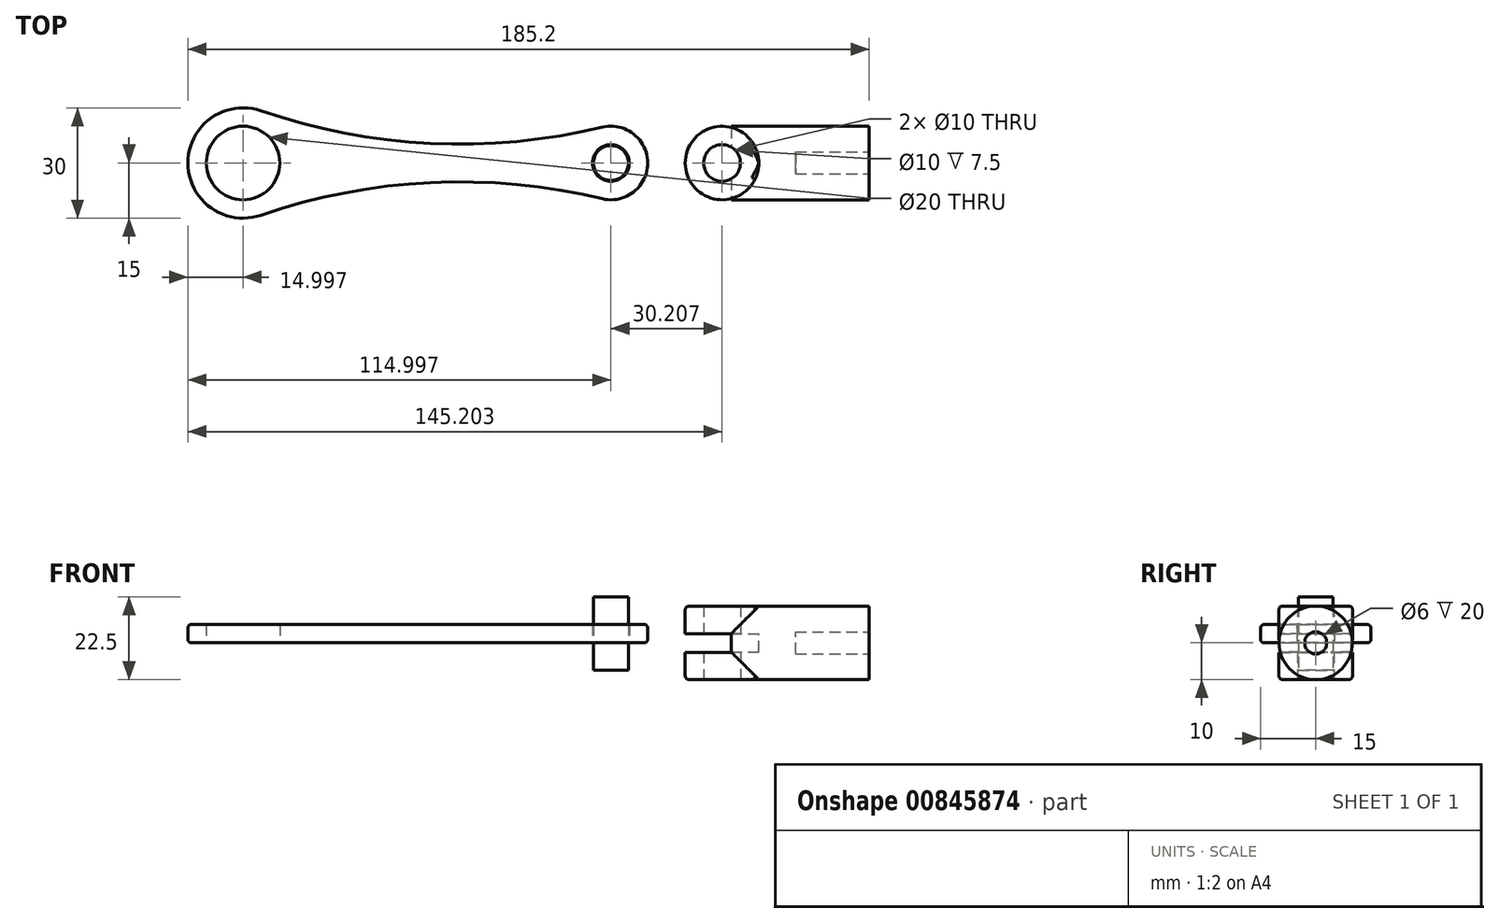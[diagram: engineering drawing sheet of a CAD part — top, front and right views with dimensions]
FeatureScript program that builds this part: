
annotation { "Feature Type Name" : "Feature", "Feature Type Description" : "" }
export const myFeature = defineFeature(function(context is Context, id is Id, definition is map)
    precondition{}
    {
        {
            var Q0;
            Q0=qCreatedBy(makeId("Top.planeOp"),FACE);
            var sketch = newSketch(context, id + "F0", { "sketchPlane" : qUnion([Q0])});
            skCircle(sketch, "E0", {"center": v(-57.77, 0) * mm, "radius": 10 * mm});
            skCircle(sketch, "E1", {"center": v(-57.77, 0) * mm, "radius": 15 * mm});
            skCircle(sketch, "E2", {"center": v(42.23, 0) * mm, "radius": 5 * mm});
            skCircle(sketch, "E3", {"center": v(42.23, 0) * mm, "radius": 10 * mm});
            skArc(sketch, "E4", {"start": v(-52.9, 14.18) * mm, "mid": v(-6.82, 5.33) * mm, "end": v(39.9, 9.72) * mm});
            skArc(sketch, "E5.MirrorCS", {"start": v(-52.9, -14.18) * mm, "mid": v(-6.82, -5.33) * mm, "end": v(39.9, -9.72) * mm});
            skCircle(sketch, "E6", {"center": v(42.23, 0) * mm, "radius": 4.75 * mm});
            skCircle(sketch, "E7", {"center": v(72.43, 0) * mm, "radius": 10 * mm});
            skCircle(sketch, "E8", {"center": v(72.43, 0) * mm, "radius": 5 * mm});
            skLineSegment(sketch, "E9", {"start": v(82.43, 0) * mm, "end": v(112.43, 0) * mm});
            skLineSegment(sketch, "E10", {"start": v(72.43, 10) * mm, "end": v(112.43, 10) * mm});
            skLineSegment(sketch, "E11", {"start": v(112.43, 10) * mm, "end": v(112.43, 0) * mm});
            skSolve(sketch);
        }
        {
            var Q0;
            Q0=makeQuery(id+"F0.imprint","IMPRINT",FACE,{"disambiguationData":[TD([[makeQuery(id+"F0.imprint","IMPRINT",EDGE,{"derivedFrom":sQuery(id+"F0.wireOp",EDGE,"E2")}),-1.0]])]});
            var Q1;
            {var subQ0=sQuery(id+"F0.wireOp",EDGE,"E4");Q1=makeQuery(id+"F0.imprint","IMPRINT",FACE,{"disambiguationData":[TD([[makeQuery(id+"F0.imprint","IMPRINT",EDGE,{"derivedFrom":subQ0}),-1.0]])]});}
            var Q2;
            Q2=makeQuery(id+"F0.imprint","IMPRINT",FACE,{"disambiguationData":[TD([[makeQuery(id+"F0.imprint","IMPRINT",EDGE,{"derivedFrom":sQuery(id+"F0.wireOp",EDGE,"E0")}),-1.0]])]});
            extrude(context, id + "F1", {"entities" : qUnion([Q0, Q1, Q2]), "depth" : 5 * mm, "offsetDistance" : 25 * mm});
        }
        {
            var Q0;
            Q0=makeQuery(id+"F1.opExtrude","CAP_EDGE",EDGE,{"disambiguationData":[OSD([sQuery(id+"F0.wireOp",EDGE,"E4")])],"isStart":false});
            var Q1;
            Q1=makeQuery(id+"F1.opExtrude","CAP_EDGE",EDGE,{"disambiguationData":[OSD([sQuery(id+"F0.wireOp",EDGE,"E1")])],"isStart":false});
            var Q2;
            Q2=makeQuery(id+"F1.opExtrude","CAP_EDGE",EDGE,{"disambiguationData":[OSD([sQuery(id+"F0.wireOp",EDGE,"E5.MirrorCS")])],"isStart":false});
            var Q3;
            Q3=makeQuery(id+"F1.opExtrude","CAP_EDGE",EDGE,{"disambiguationData":[OSD([sQuery(id+"F0.wireOp",EDGE,"E3")])],"isStart":false});
            fillet(context, id + "F2", {"entities" : qUnion([Q0, Q1, Q2, Q3]), "radius" : 1 * mm, "tangentPropagation" : true, "allowEdgeOverflow" : false});
        }
        {
            var Q0;
            Q0=makeQuery(id+"F1.opExtrude","CAP_EDGE",EDGE,{"disambiguationData":[OSD([sQuery(id+"F0.wireOp",EDGE,"E4")])],"isStart":true});
            var Q1;
            Q1=makeQuery(id+"F1.opExtrude","CAP_EDGE",EDGE,{"disambiguationData":[OSD([sQuery(id+"F0.wireOp",EDGE,"E1")])],"isStart":true});
            var Q2;
            Q2=makeQuery(id+"F1.opExtrude","CAP_EDGE",EDGE,{"disambiguationData":[OSD([sQuery(id+"F0.wireOp",EDGE,"E5.MirrorCS")])],"isStart":true});
            var Q3;
            Q3=makeQuery(id+"F1.opExtrude","CAP_EDGE",EDGE,{"disambiguationData":[OSD([sQuery(id+"F0.wireOp",EDGE,"E3")])],"isStart":true});
            fillet(context, id + "F3", {"entities" : qUnion([Q0, Q1, Q2, Q3]), "radius" : 1 * mm, "tangentPropagation" : true, "allowEdgeOverflow" : false});
        }
        {
            var Q0;
            Q0=makeQuery(id+"F0.imprint","IMPRINT",FACE,{"disambiguationData":[TD([[makeQuery(id+"F0.imprint","IMPRINT",EDGE,{"derivedFrom":sQuery(id+"F0.wireOp",EDGE,"E6")}),1.0]])]});
            extrude(context, id + "F4", {"entities" : qUnion([Q0]), "depth" : 12.5 * mm, "offsetDistance" : 25 * mm, "hasSecondDirection" : true, "secondDirectionOppositeDirection" : true, "secondDirectionDepth" : 7.5 * mm});
        }
        {
            var Q0;
            Q0=makeQuery(id+"F0.imprint","IMPRINT",FACE,{"disambiguationData":[TD([[makeQuery(id+"F0.imprint","IMPRINT",EDGE,{"derivedFrom":sQuery(id+"F0.wireOp",EDGE,"E8")}),-1.0]])]});
            extrude(context, id + "F5", {"entities" : qUnion([Q0]), "depth" : 2.5 * mm, "offsetDistance" : 25 * mm, "hasSecondDirection" : true, "secondDirectionOppositeDirection" : true, "secondDirectionDepth" : 2.5 * mm});
        }
        {
            var Q0;
            Q0=makeQuery(id+"F5.opExtrude","CAP_FACE",FACE,{"disambiguationData":[OSD([sQuery(id+"F0.wireOp",EDGE,"E7"),sQuery(id+"F0.wireOp",EDGE,"E8")])],"isStart":false});
            extrude(context, id + "F6", {"entities" : qUnion([Q0]), "depth" : 7.5 * mm, "offsetDistance" : 25 * mm});
        }
        {
            var Q0;
            Q0=makeQuery(id+"F5.opExtrude","CAP_FACE",FACE,{"disambiguationData":[OSD([sQuery(id+"F0.wireOp",EDGE,"E7"),sQuery(id+"F0.wireOp",EDGE,"E8")])],"isStart":true});
            extrude(context, id + "F7", {"entities" : qUnion([Q0]), "operationType" : NewBodyOperationType.ADD, "depth" : 7.5 * mm, "offsetDistance" : 25 * mm});
        }
        {
            var Q0;
            {var subQ0=sQuery(id+"F0.wireOp",EDGE,"E9");Q0=makeQuery(id+"F0.imprint","IMPRINT",FACE,{"disambiguationData":[TD([[makeQuery(id+"F0.imprint","IMPRINT",EDGE,{"derivedFrom":subQ0}),1.0]])]});}
            var Q1;
            Q1=sQuery(id+"F0.wireOp",EDGE,"E9");
            revolve(context, id + "F8", {"operationType" : NewBodyOperationType.ADD, "surfaceOperationType" : NewSurfaceOperationType.NEW, "entities" : qUnion([Q0]), "axis" : qUnion([Q1]), "revolveType" : RevolveType.FULL});
        }
        {
            var Q0;
            Q0=makeQuery(id+"F0.imprint","IMPRINT",FACE,{"disambiguationData":[TD([[makeQuery(id+"F0.imprint","IMPRINT",EDGE,{"derivedFrom":sQuery(id+"F0.wireOp",EDGE,"E8")}),-1.0]])]});
            extrude(context, id + "F9", {"entities" : qUnion([Q0]), "operationType" : NewBodyOperationType.REMOVE, "oppositeDirection" : true, "depth" : 2.5 * mm, "offsetDistance" : 25 * mm, "hasSecondDirection" : true, "secondDirectionOppositeDirection" : false, "secondDirectionDepth" : 2.5 * mm});
        }
        {
            var Q0;
            Q0=qCreatedBy(makeId("Front.planeOp"),FACE);
            cPlane(context, id + "F10", {"entities" : qUnion([Q0]), "cplaneType" : CPlaneType.OFFSET, "offset" : 10 * mm, "width" : 150 * mm, "height" : 150 * mm});
        }
        {
            var Q0;
            Q0=qCreatedBy(id+"F10.planeOp",FACE);
            var sketch = newSketch(context, id + "F11", { "sketchPlane" : qUnion([Q0])});
            skLineSegment(sketch, "E12", {"start": v(74.9, 2.43) * mm, "end": v(74.9, -2.57) * mm});
            skLineSegment(sketch, "E13", {"start": v(74.9, 2.43) * mm, "end": v(58.01, 2.43) * mm});
            skLineSegment(sketch, "E14", {"start": v(58.01, 2.43) * mm, "end": v(58.01, -2.57) * mm});
            skLineSegment(sketch, "E15", {"start": v(58.01, -2.57) * mm, "end": v(74.9, -2.57) * mm});
            skSolve(sketch);
        }
        {
            var Q0;
            Q0=makeQuery(id+"F11.imprint","IMPRINT",FACE,{"disambiguationData":[TD([[makeQuery(id+"F11.imprint","IMPRINT",EDGE,{"derivedFrom":sQuery(id+"F11.wireOp",EDGE,"E12")}),-1.0]])]});
            extrude(context, id + "F12", {"entities" : qUnion([Q0]), "operationType" : NewBodyOperationType.REMOVE, "oppositeDirection" : true, "depth" : 20 * mm, "offsetDistance" : 25 * mm});
        }
        {
            var Q0;
            Q0=makeQuery(id+"F0.imprint","IMPRINT",FACE,{"disambiguationData":[TD([[makeQuery(id+"F0.imprint","IMPRINT",EDGE,{"derivedFrom":sQuery(id+"F0.wireOp",EDGE,"E8")}),1.0]])]});
            extrude(context, id + "F13", {"entities" : qUnion([Q0]), "operationType" : NewBodyOperationType.REMOVE, "depth" : 10 * mm, "offsetDistance" : 25 * mm, "hasSecondDirection" : true, "secondDirectionOppositeDirection" : true, "secondDirectionDepth" : 10 * mm});
        }
        {
            var Q0;
            Q0=makeQuery(id+"F6.opExtrude","CAP_EDGE",EDGE,{"disambiguationData":[OSD([sQuery(id+"F0.wireOp",EDGE,"E7")])],"isStart":false});
            fillet(context, id + "F14", {"entities" : qUnion([Q0]), "radius" : 1 * mm, "tangentPropagation" : true, "allowEdgeOverflow" : false});
        }
        {
            var Q0;
            Q0=makeQuery(id+"F7.opExtrude","CAP_EDGE",EDGE,{"disambiguationData":[OSD([sQuery(id+"F0.wireOp",EDGE,"E7")])],"isStart":false});
            fillet(context, id + "F15", {"entities" : qUnion([Q0]), "radius" : 1 * mm, "tangentPropagation" : true, "allowEdgeOverflow" : false});
        }
        {
            var Q0;
            Q0=makeQuery(id+"F8.opRevolve","SWEPT_FACE",FACE,{"disambiguationData":[OSD([sQuery(id+"F0.wireOp",EDGE,"E11")])]});
            var sketch = newSketch(context, id + "F16", { "sketchPlane" : qUnion([Q0])});
            skCircle(sketch, "E16", {"center": v(0, 0) * mm, "radius": 3 * mm});
            skCircle(sketch, "E17.0", {"center": v(0, 0) * mm, "radius": 10 * mm});
            skSolve(sketch);
        }
        {
            var Q0;
            Q0=makeQuery(id+"F16.imprint","IMPRINT",FACE,{"disambiguationData":[TD([[makeQuery(id+"F16.imprint","IMPRINT",EDGE,{"derivedFrom":sQuery(id+"F16.wireOp",EDGE,"E16")}),1.0]])]});
            extrude(context, id + "F17", {"entities" : qUnion([Q0]), "operationType" : NewBodyOperationType.REMOVE, "oppositeDirection" : true, "depth" : 20 * mm, "offsetDistance" : 25 * mm});
        }
    });
